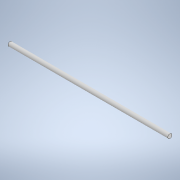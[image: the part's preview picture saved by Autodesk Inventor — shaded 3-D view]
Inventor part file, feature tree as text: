
AUTODESK INVENTOR PART (.ipt)
format: ipt  version: 2021 (Build 250183000, 183)  size: 91,648 bytes
history: native  units: in
note: dims shown in document units (in); Inventor stores cm internally (conversion verified against a paired STEP export)
features: extrude x1, sketch x1
ambient origin geometry x8: Origin, YZ Plane, XZ Plane, XY Plane, X Axis, Y Axis, Z Axis, Center Point
bodies: Solid1 (feature_tree)
feature tree (2):
  extrude  "Extrusion1"  Depth=9.5in TaperAngle=0.0deg
  sketch  "Sketch1"  dims[d0=0.25in d1=9.5in d2=0.0in]
